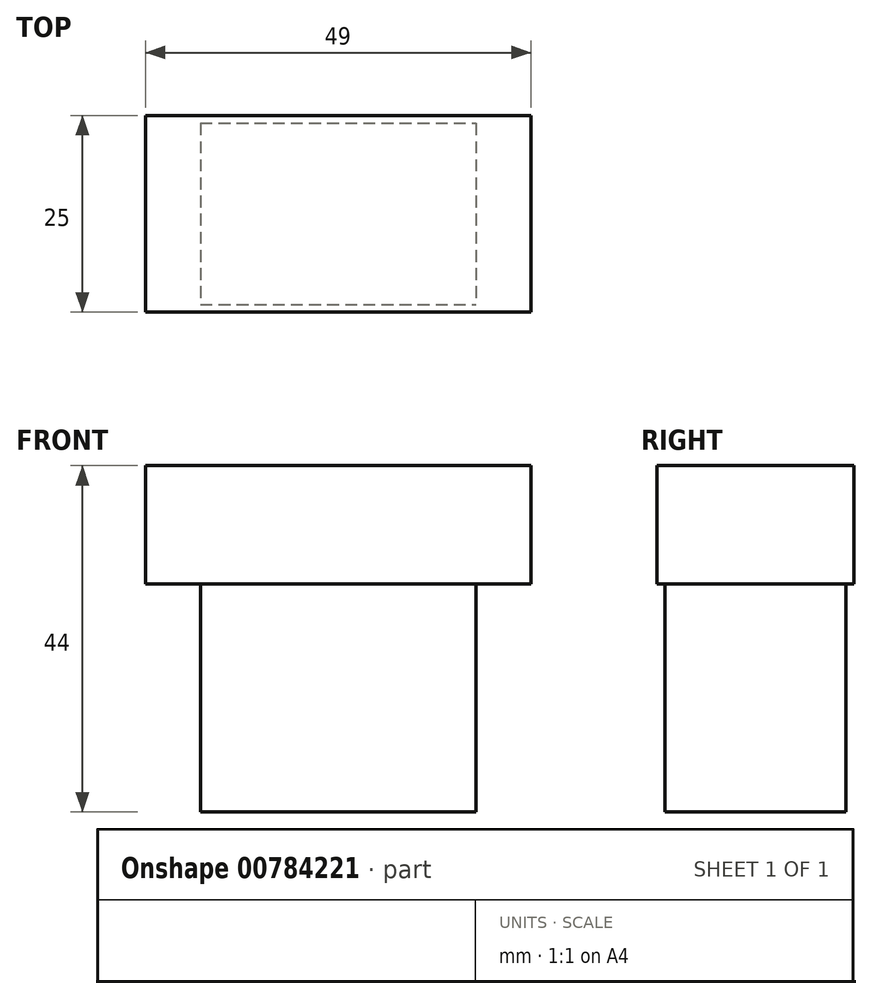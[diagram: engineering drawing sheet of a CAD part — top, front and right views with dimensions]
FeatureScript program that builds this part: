
annotation { "Feature Type Name" : "Feature", "Feature Type Description" : "" }
export const myFeature = defineFeature(function(context is Context, id is Id, definition is map)
    precondition{}
    {
        {
            var Q0;
            Q0=qCreatedBy(makeId("Top.planeOp"),FACE);
            var sketch = newSketch(context, id + "F0", { "sketchPlane" : qUnion([Q0])});
            skLineSegment(sketch, "E0.bottom", {"start": v(-10.58, 19.93) * mm, "end": v(24.42, 19.93) * mm});
            skLineSegment(sketch, "E0.top", {"start": v(-10.58, -3.07) * mm, "end": v(24.42, -3.07) * mm});
            skLineSegment(sketch, "E0.left", {"start": v(-10.58, 19.93) * mm, "end": v(-10.58, -3.07) * mm});
            skLineSegment(sketch, "E0.right", {"start": v(24.42, 19.93) * mm, "end": v(24.42, -3.07) * mm});
            skSolve(sketch);
        }
        {
            var Q0;
            Q0=makeQuery(id+"F0.imprint","IMPRINT",FACE,{"disambiguationData":[TD([[makeQuery(id+"F0.imprint","IMPRINT",EDGE,{"derivedFrom":sQuery(id+"F0.wireOp",EDGE,"E0.bottom")}),-1.0]])]});
            extrude(context, id + "F1", {"entities" : qUnion([Q0]), "depth" : 29 * mm, "offsetDistance" : 25.4 * mm});
        }
        {
            var Q0;
            Q0=makeQuery(id+"F1.opExtrude","CAP_FACE",FACE,{"disambiguationData":[OSD([sQuery(id+"F0.wireOp",EDGE,"E0.bottom"),sQuery(id+"F0.wireOp",EDGE,"E0.top"),sQuery(id+"F0.wireOp",EDGE,"E0.left"),sQuery(id+"F0.wireOp",EDGE,"E0.right")])],"isStart":false});
            var sketch = newSketch(context, id + "F2", { "sketchPlane" : qUnion([Q0])});
            skLineSegment(sketch, "E1.bottom", {"start": v(-17.58, 20.93) * mm, "end": v(31.42, 20.93) * mm});
            skLineSegment(sketch, "E1.top", {"start": v(-17.58, -4.07) * mm, "end": v(31.42, -4.07) * mm});
            skLineSegment(sketch, "E1.left", {"start": v(-17.58, 20.93) * mm, "end": v(-17.58, -4.07) * mm});
            skLineSegment(sketch, "E1.right", {"start": v(31.42, 20.93) * mm, "end": v(31.42, -4.07) * mm});
            skSolve(sketch);
        }
        {
            var Q0;
            Q0=makeQuery(id+"F2.imprint","IMPRINT",FACE,{"disambiguationData":[TD([[makeQuery(id+"F2.imprint","IMPRINT",EDGE,{"derivedFrom":makeQuery(id+"F1.opExtrude","CAP_EDGE",EDGE,{"disambiguationData":[OSD([sQuery(id+"F0.wireOp",EDGE,"E0.bottom")])],"isStart":false})}),-1.0]])]});
            var Q1;
            Q1=makeQuery(id+"F2.imprint","IMPRINT",FACE,{"disambiguationData":[TD([[makeQuery(id+"F2.imprint","IMPRINT",EDGE,{"derivedFrom":sQuery(id+"F2.wireOp",EDGE,"E1.bottom")}),-1.0]])]});
            extrude(context, id + "F3", {"entities" : qUnion([Q0, Q1]), "operationType" : NewBodyOperationType.ADD, "depth" : 15 * mm, "offsetDistance" : 25.4 * mm});
        }
    });
